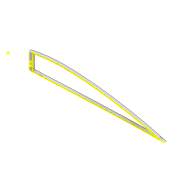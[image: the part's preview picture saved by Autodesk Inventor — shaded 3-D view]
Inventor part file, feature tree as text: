
AUTODESK INVENTOR PART (.ipt)
format: ipt  version: 2022 (Build 260153000, 153)  size: 287,744 bytes
history: native  units: mm
features: sketch x7, extrude x6, thicken_offset x4, projected_geometry x4, shell x1, fillet x1
ambient origin geometry x8: Origin, YZ Plane, XZ Plane, XY Plane, X Axis, Y Axis, Z Axis, Center Point
bodies: Solid1 (feature_tree)
feature tree (23):
  extrude  "Extrusion1"  Depth=5.0mm
  shell  "Shell1"  Thickness=6.0mm
  extrude  "Extrusion2"  Depth=2.0mm
  extrude  "Extrusion3"  Depth=5.9mm
  extrude  "Extrusion4"  Depth=10.0mm TaperAngle=0.0deg
  extrude  "Extrusion7"  Depth=10.0mm TaperAngle=0.0deg
  thicken_offset  "Thicken1"
  thicken_offset  "Thicken2"
  extrude  "Extrusion8"  Depth=2.0mm
  fillet  "Fillet1"  Radius=4.5mm
  thicken_offset  "Thicken4"
  thicken_offset  "Thicken5"
  sketch  "Sketch17"  dims[d31=3.0mm d32=3.0mm d33=3.0mm d34=3.0mm d35=1.0mm d36=10.0mm d37=0.0mm d38=2.0mm d42=0.2mm d43=0.2mm d44=0.2mm d45=0.2mm]
  sketch  "Sketch3"  dims[d0=4.5mm d1=0.0mm d2=5.0mm d3=6.0mm]
  sketch  "Sketch7"  dims[d5=4.5mm d6=0.0mm d7=2.0mm]
  projected_geometry  "Projected Loop3"
  sketch  "Sketch8"  dims[d8=2.0mm d9=5.9mm]
  sketch  "Sketch9"  dims[d12=4.0mm d13=10.0mm d14=0.0mm]
  sketch  "Sketch14"  dims[d15=40.0mm d16=10.0mm d17=0.0mm]
  projected_geometry  "Projected Loop7"
  sketch  "Sketch16"  dims[d24=2.0mm d26=2.0mm d29=4.5mm d30=0.0mm]
  projected_geometry  "Projected Loop9"
  projected_geometry  "Projected Loop10"
